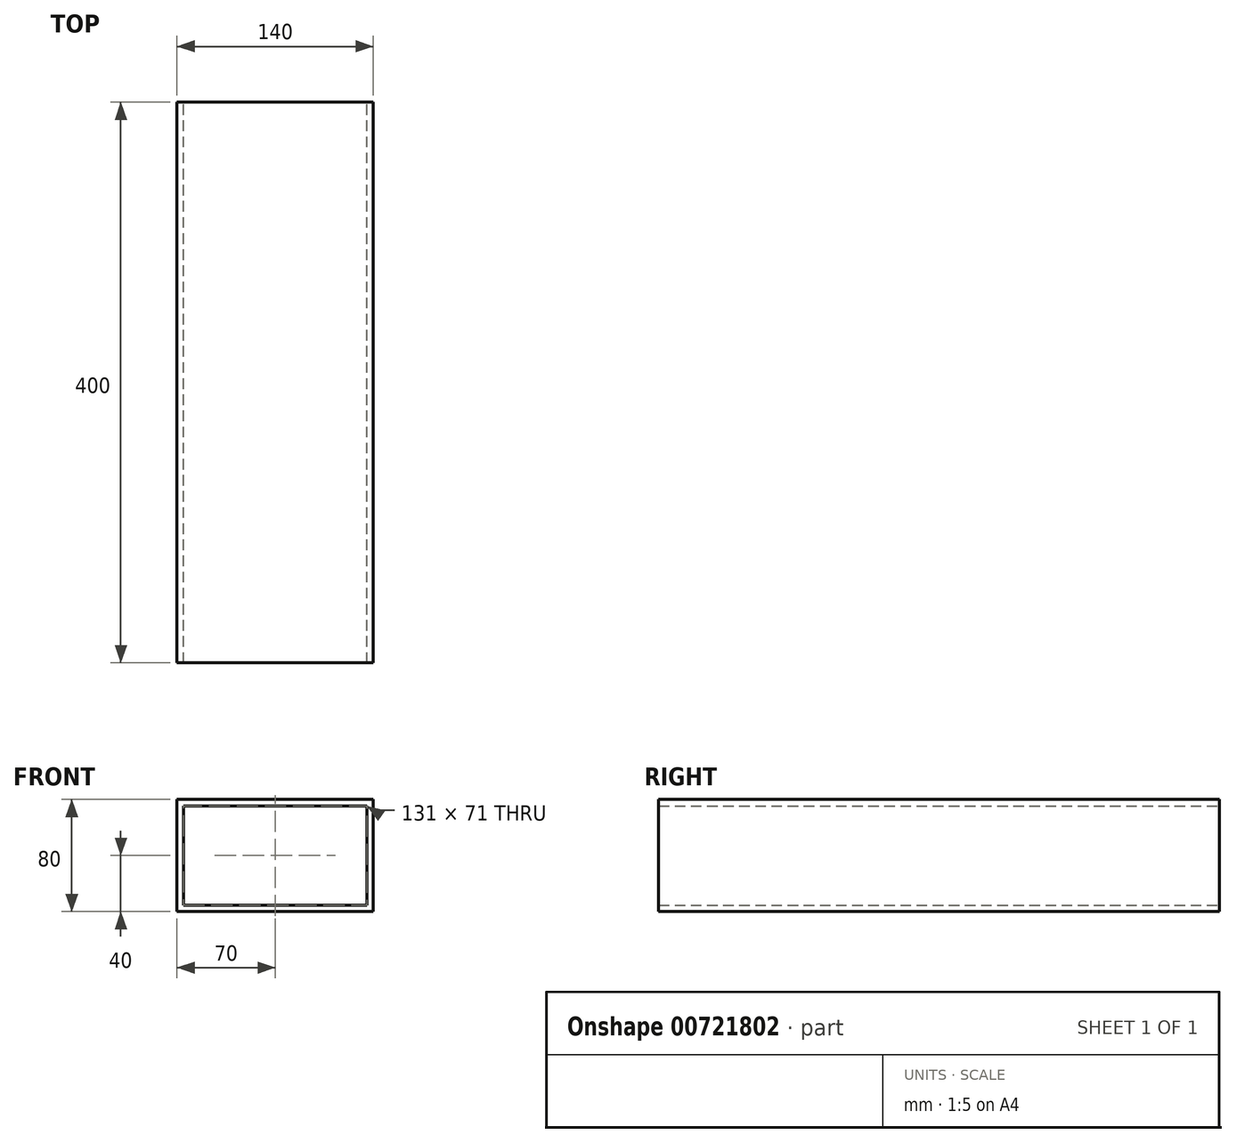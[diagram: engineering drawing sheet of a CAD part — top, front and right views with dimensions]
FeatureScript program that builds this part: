
annotation { "Feature Type Name" : "Feature", "Feature Type Description" : "" }
export const myFeature = defineFeature(function(context is Context, id is Id, definition is map)
    precondition{}
    {
        {
            var Q0;
            Q0=qCreatedBy(makeId("Front.planeOp"),FACE);
            var sketch = newSketch(context, id + "F0", { "sketchPlane" : qUnion([Q0])});
            skLineSegment(sketch, "E0.bottom", {"start": v(70, -40) * mm, "end": v(-70, -40) * mm});
            skLineSegment(sketch, "E0.top", {"start": v(70, 40) * mm, "end": v(-70, 40) * mm});
            skLineSegment(sketch, "E0.left", {"start": v(70, -40) * mm, "end": v(70, 40) * mm});
            skLineSegment(sketch, "E0.right", {"start": v(-70, -40) * mm, "end": v(-70, 40) * mm});
            skPoint(sketch, "E0.middle", {"position": v(0, 0) * mm});
            skLineSegment(sketch, "E1.bottom", {"start": v(65.5, -35.5) * mm, "end": v(-65.5, -35.5) * mm});
            skLineSegment(sketch, "E1.top", {"start": v(65.5, 35.5) * mm, "end": v(-65.5, 35.5) * mm});
            skLineSegment(sketch, "E1.left", {"start": v(65.5, -35.5) * mm, "end": v(65.5, 35.5) * mm});
            skLineSegment(sketch, "E1.right", {"start": v(-65.5, -35.5) * mm, "end": v(-65.5, 35.5) * mm});
            skSolve(sketch);
        }
        {
            var Q0;
            Q0 = qSketchRegion(id + "F0", true);
            extrude(context, id + "F1", {"entities" : qUnion([Q0]), "depth" : 400 * mm, "offsetDistance" : 25 * mm});
        }
    });
